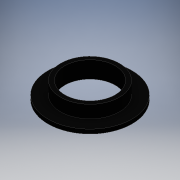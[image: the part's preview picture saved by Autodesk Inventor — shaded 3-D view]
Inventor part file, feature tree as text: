
AUTODESK INVENTOR PART (.ipt)
format: ipt  version: 2016 (Build 200138000, 138)  size: 103,424 bytes
history: native  units: mm
features: extrude x2, other x1, sketch x1
ambient origin geometry x8: Origin, YZ Plane, XZ Plane, XY Plane, X Axis, Y Axis, Z Axis, Center Point
bodies: Body1 (feature_tree)
feature tree (4):
  other  "ソリッド1"
  sketch  "スケッチ1"
  extrude  "押し出し1"  Depth=12.0mm
  extrude  "押し出し2"  Depth=14.0mm
